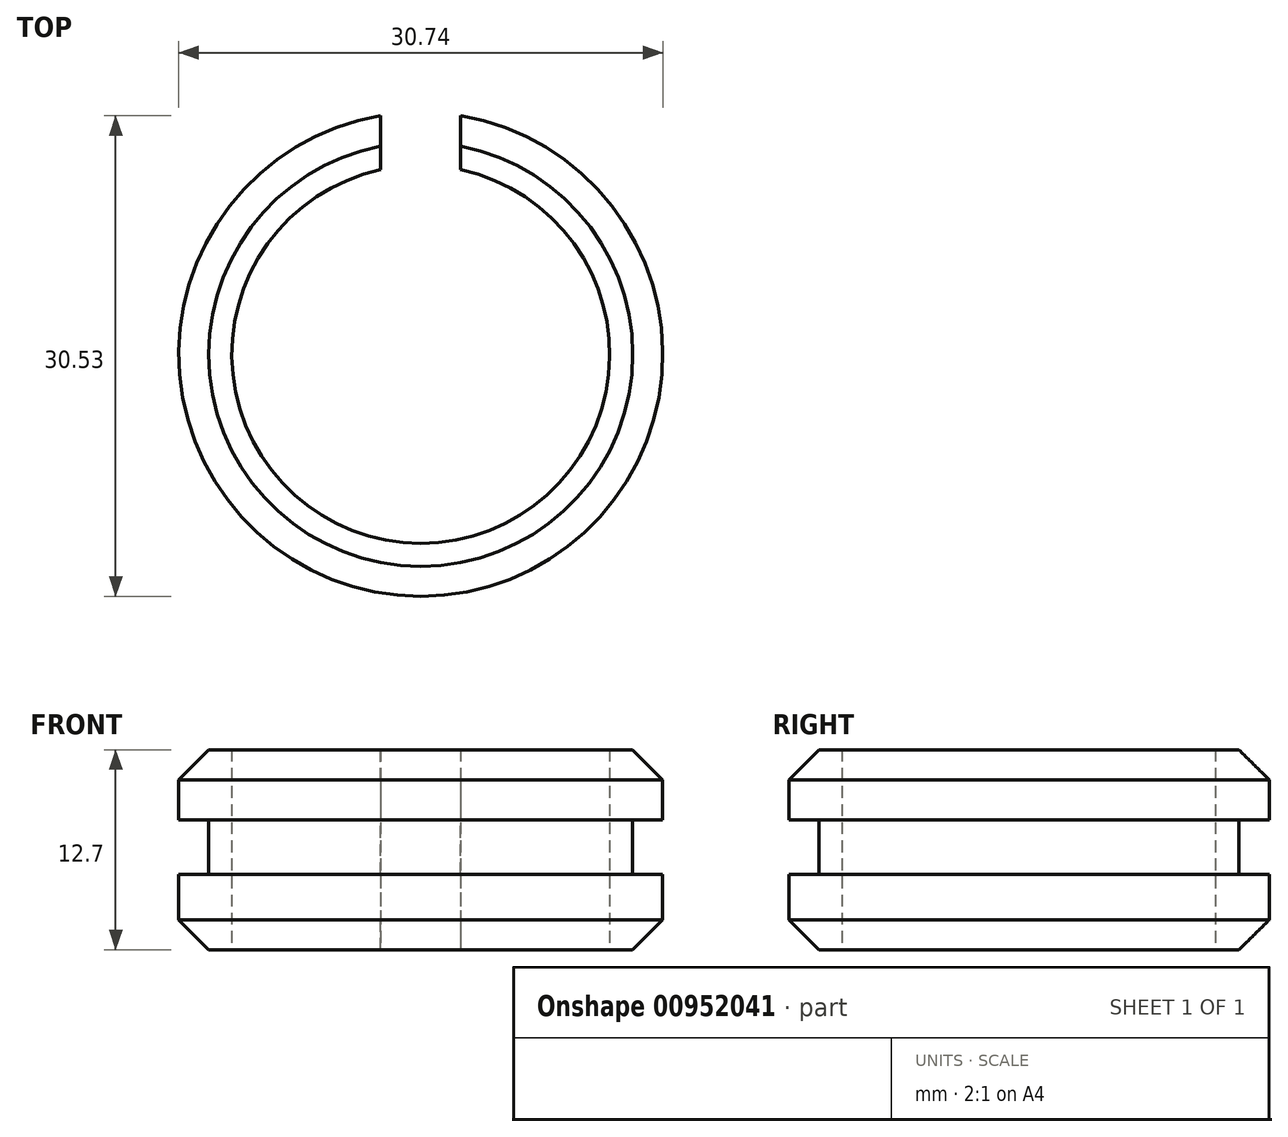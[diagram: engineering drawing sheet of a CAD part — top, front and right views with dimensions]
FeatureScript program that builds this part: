
annotation { "Feature Type Name" : "Feature", "Feature Type Description" : "" }
export const myFeature = defineFeature(function(context is Context, id is Id, definition is map)
    precondition{}
    {
        {
            var Q0;
            Q0=qCreatedBy(makeId("Top.planeOp"),FACE);
            var sketch = newSketch(context, id + "F0", { "sketchPlane" : qUnion([Q0])});
            skArc(sketch, "E0", {"start": v(-2.54, 11.73) * mm, "mid": v(0, -12) * mm, "end": v(2.54, 11.73) * mm});
            skArc(sketch, "E1", {"start": v(-2.54, 15.16) * mm, "mid": v(0, -15.37) * mm, "end": v(2.54, 15.16) * mm});
            skLineSegment(sketch, "E2", {"start": v(-2.54, 15.16) * mm, "end": v(-2.54, 11.73) * mm});
            skLineSegment(sketch, "E3.MirrorCS", {"start": v(2.54, 15.16) * mm, "end": v(2.54, 11.73) * mm});
            skSolve(sketch);
        }
        {
            var Q0;
            Q0=makeQuery(id+"F0.imprint","IMPRINT",FACE,{"disambiguationData":[TD([[makeQuery(id+"F0.imprint","IMPRINT",EDGE,{"derivedFrom":sQuery(id+"F0.wireOp",EDGE,"E0")}),-1.0]])]});
            extrude(context, id + "F1", {"entities" : qUnion([Q0]), "depth" : 12.7 * mm, "offsetDistance" : 25.4 * mm});
        }
        {
            var Q0;
            Q0=qCreatedBy(makeId("Front.planeOp"),FACE);
            var sketch = newSketch(context, id + "F2", { "sketchPlane" : qUnion([Q0])});
            skLineSegment(sketch, "E4.bottom", {"start": v(15.58, 8.26) * mm, "end": v(13.46, 8.26) * mm});
            skLineSegment(sketch, "E4.top", {"start": v(15.58, 4.8) * mm, "end": v(13.46, 4.8) * mm});
            skLineSegment(sketch, "E4.left", {"start": v(15.58, 8.26) * mm, "end": v(15.58, 4.8) * mm});
            skLineSegment(sketch, "E4.right", {"start": v(13.46, 8.26) * mm, "end": v(13.46, 4.8) * mm});
            skLineSegment(sketch, "E5", {"start": v(0, 13.12) * mm, "end": v(0, 0.89) * mm, "construction": true});
            skSolve(sketch);
        }
        {
            var Q0;
            Q0 = qSketchRegion(id + "F2", true);
            var Q1;
            Q1=sQuery(id+"F2.wireOp",EDGE,"E5");
            revolve(context, id + "F3", {"operationType" : NewBodyOperationType.REMOVE, "surfaceOperationType" : NewSurfaceOperationType.NEW, "entities" : qUnion([Q0]), "axis" : qUnion([Q1]), "revolveType" : RevolveType.FULL});
        }
        {
            var Q0;
            Q0=makeQuery(id+"F1.opExtrude","CAP_EDGE",EDGE,{"disambiguationData":[OSD([sQuery(id+"F0.wireOp",EDGE,"E1")])],"isStart":false});
            var Q1;
            Q1=makeQuery(id+"F1.opExtrude","CAP_EDGE",EDGE,{"disambiguationData":[OSD([sQuery(id+"F0.wireOp",EDGE,"E1")])],"isStart":true});
            chamfer(context, id + "F4", {"entities" : qUnion([Q0, Q1]), "width" : 1.9 * mm, "tangentPropagation" : true});
        }
    });
